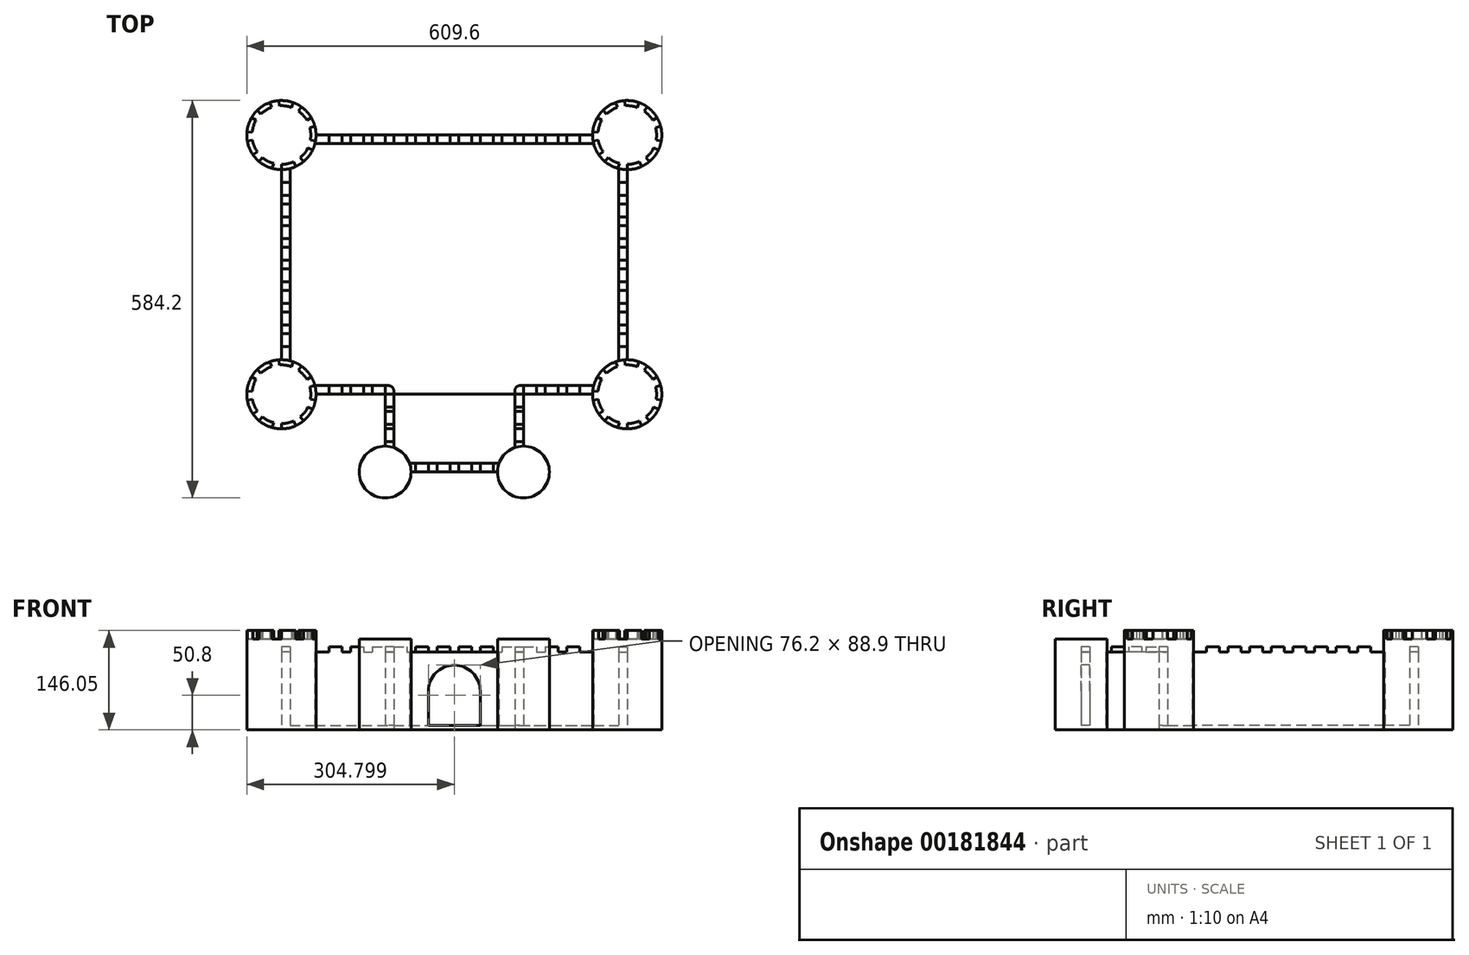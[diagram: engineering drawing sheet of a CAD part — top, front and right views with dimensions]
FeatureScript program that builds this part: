
annotation { "Feature Type Name" : "Feature", "Feature Type Description" : "" }
export const myFeature = defineFeature(function(context is Context, id is Id, definition is map)
    precondition{}
    {
        {
            var Q0;
            Q0=qCreatedBy(makeId("Top.planeOp"),FACE);
            var sketch = newSketch(context, id + "F0", { "sketchPlane" : qUnion([Q0])});
            skLineSegment(sketch, "E0.bottom", {"start": v(-131.16, 291.62) * mm, "end": v(376.84, 291.62) * mm});
            skLineSegment(sketch, "E0.top", {"start": v(-131.16, -89.38) * mm, "end": v(376.84, -89.38) * mm});
            skLineSegment(sketch, "E0.left", {"start": v(-131.16, 291.62) * mm, "end": v(-131.16, -89.38) * mm});
            skLineSegment(sketch, "E0.right", {"start": v(376.84, 291.62) * mm, "end": v(376.84, -89.38) * mm});
            skCircle(sketch, "E1", {"center": v(-131.16, 291.62) * mm, "radius": 50.8 * mm});
            skCircle(sketch, "E2", {"center": v(376.84, 291.62) * mm, "radius": 50.8 * mm});
            skCircle(sketch, "E3", {"center": v(-131.16, -89.38) * mm, "radius": 50.8 * mm});
            skCircle(sketch, "E4", {"center": v(376.84, -89.38) * mm, "radius": 50.8 * mm});
            skLineSegment(sketch, "E5.bottom", {"start": v(21.24, -89.38) * mm, "end": v(224.44, -89.38) * mm});
            skLineSegment(sketch, "E5.top", {"start": v(21.24, -203.68) * mm, "end": v(224.44, -203.68) * mm});
            skLineSegment(sketch, "E5.left", {"start": v(21.24, -89.38) * mm, "end": v(21.24, -203.68) * mm});
            skLineSegment(sketch, "E5.right", {"start": v(224.44, -89.38) * mm, "end": v(224.44, -203.68) * mm});
            skCircle(sketch, "E6", {"center": v(21.24, -203.68) * mm, "radius": 38.1 * mm});
            skCircle(sketch, "E7", {"center": v(224.44, -203.68) * mm, "radius": 38.1 * mm});
            skLineSegment(sketch, "E8.bottom", {"start": v(33.94, -89.38) * mm, "end": v(211.74, -89.38) * mm});
            skLineSegment(sketch, "E8.top", {"start": v(33.94, -190.98) * mm, "end": v(211.74, -190.98) * mm});
            skLineSegment(sketch, "E8.left", {"start": v(33.94, -89.38) * mm, "end": v(33.94, -190.98) * mm});
            skLineSegment(sketch, "E8.right", {"start": v(211.74, -89.38) * mm, "end": v(211.74, -190.98) * mm});
            skSolve(sketch);
        }
        {
            var Q0;
            {var subQ5=sQuery(id+"F0.wireOp",EDGE,"E1");var subQ10=sQuery(id+"F0.wireOp",EDGE,"E0.bottom");var subQ15=makeQuery(id+"F0.imprint","INTERSECT",VERTEX,{"derivedFrom":[subQ10,subQ5]});Q0=makeQuery(id+"F0.imprint","IMPRINT",FACE,{"disambiguationData":[TD([[makeQuery(id+"F0.imprint","IMPRINT",EDGE,{"disambiguationData":[TD([[subQ15,-1.0]])],"derivedFrom":subQ10}),-1.0]])]});}
            var Q1;
            {var subQ5=sQuery(id+"F0.wireOp",EDGE,"E8.bottom");Q1=makeQuery(id+"F0.imprint","IMPRINT",FACE,{"disambiguationData":[TD([[makeQuery(id+"F0.imprint","IMPRINT",EDGE,{"derivedFrom":subQ5}),-1.0]])]});}
            extrude(context, id + "F1", {"entities" : qUnion([Q0, Q1]), "depth" : 6.35 * mm});
        }
        {
            var Q0;
            {var subQ0=sQuery(id+"F0.wireOp",EDGE,"E0.left");var subQ1=sQuery(id+"F0.wireOp",EDGE,"E0.bottom");var subQ2=makeQuery(id+"F0.imprint","INTERSECT",VERTEX,{"derivedFrom":[subQ1,subQ0]});Q0=makeQuery(id+"F0.imprint","IMPRINT",FACE,{"disambiguationData":[TD([[makeQuery(id+"F0.imprint","IMPRINT",EDGE,{"disambiguationData":[TD([[subQ2,-1.0]])],"derivedFrom":subQ1}),1.0]])]});}
            var Q1;
            {var subQ0=sQuery(id+"F0.wireOp",EDGE,"E0.left");var subQ1=sQuery(id+"F0.wireOp",EDGE,"E0.bottom");var subQ2=makeQuery(id+"F0.imprint","INTERSECT",VERTEX,{"derivedFrom":[subQ1,subQ0]});Q1=makeQuery(id+"F0.imprint","IMPRINT",FACE,{"disambiguationData":[TD([[makeQuery(id+"F0.imprint","IMPRINT",EDGE,{"disambiguationData":[TD([[subQ2,-1.0]])],"derivedFrom":subQ1}),-1.0]])]});}
            var Q2;
            {var subQ0=sQuery(id+"F0.wireOp",EDGE,"E0.left");var subQ1=sQuery(id+"F0.wireOp",EDGE,"E0.top");var subQ2=makeQuery(id+"F0.imprint","INTERSECT",VERTEX,{"derivedFrom":[subQ1,subQ0]});Q2=makeQuery(id+"F0.imprint","IMPRINT",FACE,{"disambiguationData":[TD([[makeQuery(id+"F0.imprint","IMPRINT",EDGE,{"disambiguationData":[TD([[subQ2,-1.0]])],"derivedFrom":subQ1}),-1.0]])]});}
            var Q3;
            {var subQ0=sQuery(id+"F0.wireOp",EDGE,"E0.left");var subQ1=sQuery(id+"F0.wireOp",EDGE,"E0.top");var subQ2=makeQuery(id+"F0.imprint","INTERSECT",VERTEX,{"derivedFrom":[subQ1,subQ0]});Q3=makeQuery(id+"F0.imprint","IMPRINT",FACE,{"disambiguationData":[TD([[makeQuery(id+"F0.imprint","IMPRINT",EDGE,{"disambiguationData":[TD([[subQ2,-1.0]])],"derivedFrom":subQ1}),1.0]])]});}
            var Q4;
            {var subQ0=sQuery(id+"F0.wireOp",EDGE,"E0.right");var subQ1=sQuery(id+"F0.wireOp",EDGE,"E0.bottom");var subQ2=makeQuery(id+"F0.imprint","INTERSECT",VERTEX,{"derivedFrom":[subQ1,subQ0]});Q4=makeQuery(id+"F0.imprint","IMPRINT",FACE,{"disambiguationData":[TD([[makeQuery(id+"F0.imprint","IMPRINT",EDGE,{"disambiguationData":[TD([[subQ2,1.0]])],"derivedFrom":subQ1}),-1.0]])]});}
            var Q5;
            {var subQ0=sQuery(id+"F0.wireOp",EDGE,"E0.right");var subQ1=sQuery(id+"F0.wireOp",EDGE,"E0.bottom");var subQ2=makeQuery(id+"F0.imprint","INTERSECT",VERTEX,{"derivedFrom":[subQ1,subQ0]});Q5=makeQuery(id+"F0.imprint","IMPRINT",FACE,{"disambiguationData":[TD([[makeQuery(id+"F0.imprint","IMPRINT",EDGE,{"disambiguationData":[TD([[subQ2,1.0]])],"derivedFrom":subQ1}),1.0]])]});}
            var Q6;
            {var subQ0=sQuery(id+"F0.wireOp",EDGE,"E0.right");var subQ1=sQuery(id+"F0.wireOp",EDGE,"E0.top");var subQ2=makeQuery(id+"F0.imprint","INTERSECT",VERTEX,{"derivedFrom":[subQ1,subQ0]});Q6=makeQuery(id+"F0.imprint","IMPRINT",FACE,{"disambiguationData":[TD([[makeQuery(id+"F0.imprint","IMPRINT",EDGE,{"disambiguationData":[TD([[subQ2,1.0]])],"derivedFrom":subQ1}),-1.0]])]});}
            var Q7;
            {var subQ0=sQuery(id+"F0.wireOp",EDGE,"E0.right");var subQ1=sQuery(id+"F0.wireOp",EDGE,"E0.top");var subQ2=makeQuery(id+"F0.imprint","INTERSECT",VERTEX,{"derivedFrom":[subQ1,subQ0]});Q7=makeQuery(id+"F0.imprint","IMPRINT",FACE,{"disambiguationData":[TD([[makeQuery(id+"F0.imprint","IMPRINT",EDGE,{"disambiguationData":[TD([[subQ2,1.0]])],"derivedFrom":subQ1}),1.0]])]});}
            extrude(context, id + "F2", {"entities" : qUnion([Q0, Q1, Q2, Q3, Q4, Q5, Q6, Q7]), "operationType" : NewBodyOperationType.ADD, "depth" : 133.35 * mm});
        }
        {
            var Q0;
            Q0=makeQuery(id+"F1.opExtrude","CAP_FACE",FACE,{"disambiguationData":[OSD([sQuery(id+"F0.wireOp",EDGE,"E0.bottom"),sQuery(id+"F0.wireOp",EDGE,"E0.top"),sQuery(id+"F0.wireOp",EDGE,"E0.left"),sQuery(id+"F0.wireOp",EDGE,"E0.right"),sQuery(id+"F0.wireOp",EDGE,"E1"),sQuery(id+"F0.wireOp",EDGE,"E2"),sQuery(id+"F0.wireOp",EDGE,"E3"),sQuery(id+"F0.wireOp",EDGE,"E4")])],"isStart":false});
            var sketch = newSketch(context, id + "F3", { "sketchPlane" : qUnion([Q0])});
            skLineSegment(sketch, "E9", {"start": v(-80.36, -89.38) * mm, "end": v(326.04, -89.38) * mm});
            skLineSegment(sketch, "E10", {"start": v(-118.46, 242.43) * mm, "end": v(-118.46, -40.2) * mm});
            skLineSegment(sketch, "E11", {"start": v(-131.16, 240.82) * mm, "end": v(-131.16, -38.58) * mm});
            skLineSegment(sketch, "E12", {"start": v(-80.36, 291.62) * mm, "end": v(326.04, 291.62) * mm});
            skLineSegment(sketch, "E13", {"start": v(-81.97, 278.92) * mm, "end": v(327.65, 278.92) * mm});
            skLineSegment(sketch, "E14", {"start": v(376.84, 240.82) * mm, "end": v(376.84, -38.58) * mm});
            skLineSegment(sketch, "E15", {"start": v(364.14, 242.43) * mm, "end": v(364.14, -40.2) * mm});
            skLineSegment(sketch, "E16", {"start": v(-81.97, -76.68) * mm, "end": v(33.94, -76.68) * mm});
            skLineSegment(sketch, "E17", {"start": v(33.94, -76.68) * mm, "end": v(33.94, -89.38) * mm});
            skLineSegment(sketch, "E18", {"start": v(211.74, -89.38) * mm, "end": v(211.74, -76.68) * mm});
            skLineSegment(sketch, "E19", {"start": v(211.74, -76.68) * mm, "end": v(327.65, -76.68) * mm});
            skSolve(sketch);
        }
        {
            var Q0;
            {var subQ0=sQuery(id+"F3.wireOp",EDGE,"E10");Q0=makeQuery(id+"F3.imprint","IMPRINT",FACE,{"disambiguationData":[TD([[makeQuery(id+"F3.imprint","IMPRINT",EDGE,{"derivedFrom":subQ0}),-1.0]])]});}
            var Q1;
            {var subQ0=sQuery(id+"F3.wireOp",EDGE,"9q2WOOh6-w2Ju-GZx3-tS78-7SEucZNv8yoA");Q1=makeQuery(id+"F3.imprint","IMPRINT",FACE,{"disambiguationData":[TD([[makeQuery(id+"F3.imprint","IMPRINT",EDGE,{"derivedFrom":subQ0}),-1.0]])]});}
            var Q2;
            {var subQ0=sQuery(id+"F3.wireOp",EDGE,"E14");Q2=makeQuery(id+"F3.imprint","IMPRINT",FACE,{"disambiguationData":[TD([[makeQuery(id+"F3.imprint","IMPRINT",EDGE,{"derivedFrom":subQ0}),-1.0]])]});}
            var Q3;
            {var subQ0=sQuery(id+"F3.wireOp",EDGE,"E12");Q3=makeQuery(id+"F3.imprint","IMPRINT",FACE,{"disambiguationData":[TD([[makeQuery(id+"F3.imprint","IMPRINT",EDGE,{"derivedFrom":subQ0}),-1.0]])]});}
            var Q4;
            {var subQ4=sQuery(id+"F3.wireOp",EDGE,"E16");Q4=makeQuery(id+"F3.imprint","IMPRINT",FACE,{"disambiguationData":[TD([[makeQuery(id+"F3.imprint","IMPRINT",EDGE,{"derivedFrom":subQ4}),-1.0]])]});}
            var Q5;
            {var subQ0=sQuery(id+"F3.wireOp",EDGE,"E18");Q5=makeQuery(id+"F3.imprint","IMPRINT",FACE,{"disambiguationData":[TD([[makeQuery(id+"F3.imprint","IMPRINT",EDGE,{"derivedFrom":subQ0}),-1.0]])]});}
            extrude(context, id + "F4", {"entities" : qUnion([Q0, Q1, Q2, Q3, Q4, Q5]), "operationType" : NewBodyOperationType.ADD, "depth" : 107.95 * mm});
        }
        {
            var Q0;
            Q0=makeQuery(id+"F4.opExtrude","CAP_FACE",FACE,{"disambiguationData":[OSD([sQuery(id+"F0.wireOp",EDGE,"E3"),sQuery(id+"F0.wireOp",EDGE,"E4"),sQuery(id+"F3.wireOp",EDGE,"9q2WOOh6-w2Ju-GZx3-tS78-7SEucZNv8yoA"),sQuery(id+"F3.wireOp",EDGE,"E9")])],"isStart":false});
            var sketch = newSketch(context, id + "F5", { "sketchPlane" : qUnion([Q0])});
            skLineSegment(sketch, "E20.bottom", {"start": v(-61.31, -76.68) * mm, "end": v(-42.26, -76.68) * mm});
            skLineSegment(sketch, "E20.top", {"start": v(-61.31, -89.38) * mm, "end": v(-42.26, -89.38) * mm});
            skLineSegment(sketch, "E20.left", {"start": v(-61.31, -76.68) * mm, "end": v(-61.31, -89.38) * mm});
            skLineSegment(sketch, "E20.right", {"start": v(-42.26, -76.68) * mm, "end": v(-42.26, -89.38) * mm});
            skLineSegment(sketch, "E21.bottom", {"start": v(-29.56, -76.68) * mm, "end": v(-10.51, -76.68) * mm});
            skLineSegment(sketch, "E21.top", {"start": v(-29.56, -89.38) * mm, "end": v(-10.51, -89.38) * mm});
            skLineSegment(sketch, "E21.left", {"start": v(-29.56, -76.68) * mm, "end": v(-29.56, -89.38) * mm});
            skLineSegment(sketch, "E21.right", {"start": v(-10.51, -76.68) * mm, "end": v(-10.51, -89.38) * mm});
            skLineSegment(sketch, "E22.bottom", {"start": v(2.19, -76.68) * mm, "end": v(21.24, -76.68) * mm});
            skLineSegment(sketch, "E22.top", {"start": v(2.19, -89.38) * mm, "end": v(21.24, -89.38) * mm});
            skLineSegment(sketch, "E22.left", {"start": v(2.19, -76.68) * mm, "end": v(2.19, -89.38) * mm});
            skLineSegment(sketch, "E22.right", {"start": v(21.24, -76.68) * mm, "end": v(21.24, -89.38) * mm});
            skLineSegment(sketch, "E23.bottom", {"start": v(224.44, -76.68) * mm, "end": v(243.49, -76.68) * mm});
            skLineSegment(sketch, "E23.top", {"start": v(224.44, -89.38) * mm, "end": v(243.49, -89.38) * mm});
            skLineSegment(sketch, "E23.left", {"start": v(224.44, -76.68) * mm, "end": v(224.44, -89.38) * mm});
            skLineSegment(sketch, "E23.right", {"start": v(243.49, -76.68) * mm, "end": v(243.49, -89.38) * mm});
            skLineSegment(sketch, "E24.bottom", {"start": v(256.19, -76.68) * mm, "end": v(275.24, -76.68) * mm});
            skLineSegment(sketch, "E24.top", {"start": v(256.19, -89.38) * mm, "end": v(275.24, -89.38) * mm});
            skLineSegment(sketch, "E24.left", {"start": v(256.19, -76.68) * mm, "end": v(256.19, -89.38) * mm});
            skLineSegment(sketch, "E24.right", {"start": v(275.24, -76.68) * mm, "end": v(275.24, -89.38) * mm});
            skLineSegment(sketch, "E25.bottom", {"start": v(287.94, -76.68) * mm, "end": v(306.99, -76.68) * mm});
            skLineSegment(sketch, "E25.top", {"start": v(287.94, -89.38) * mm, "end": v(306.99, -89.38) * mm});
            skLineSegment(sketch, "E25.left", {"start": v(287.94, -76.68) * mm, "end": v(287.94, -89.38) * mm});
            skLineSegment(sketch, "E25.right", {"start": v(306.99, -76.68) * mm, "end": v(306.99, -89.38) * mm});
            skSolve(sketch);
        }
        {
            var Q0;
            Q0 = qSketchRegion(id + "F5", true);
            extrude(context, id + "F6", {"entities" : qUnion([Q0]), "operationType" : NewBodyOperationType.ADD, "depth" : 7.62 * mm});
        }
        {
            var Q0;
            Q0=makeQuery(id+"F4.opExtrude","CAP_FACE",FACE,{"disambiguationData":[OSD([sQuery(id+"F0.wireOp",EDGE,"E1"),sQuery(id+"F0.wireOp",EDGE,"E3"),sQuery(id+"F3.wireOp",EDGE,"E10"),sQuery(id+"F3.wireOp",EDGE,"E11")])],"isStart":false});
            var sketch = newSketch(context, id + "F7", { "sketchPlane" : qUnion([Q0])});
            skLineSegment(sketch, "E26.bottom", {"start": v(-118.46, 221.77) * mm, "end": v(-131.16, 221.77) * mm});
            skLineSegment(sketch, "E26.top", {"start": v(-118.46, 202.72) * mm, "end": v(-131.16, 202.72) * mm});
            skLineSegment(sketch, "E26.left", {"start": v(-118.46, 221.77) * mm, "end": v(-118.46, 202.72) * mm});
            skLineSegment(sketch, "E26.right", {"start": v(-131.16, 221.77) * mm, "end": v(-131.16, 202.72) * mm});
            skLineSegment(sketch, "E27.bottom", {"start": v(-118.46, 190.02) * mm, "end": v(-131.16, 190.02) * mm});
            skLineSegment(sketch, "E27.top", {"start": v(-118.46, 170.97) * mm, "end": v(-131.16, 170.97) * mm});
            skLineSegment(sketch, "E27.left", {"start": v(-118.46, 190.02) * mm, "end": v(-118.46, 170.97) * mm});
            skLineSegment(sketch, "E27.right", {"start": v(-131.16, 190.02) * mm, "end": v(-131.16, 170.97) * mm});
            skLineSegment(sketch, "E28.bottom", {"start": v(-118.46, 158.27) * mm, "end": v(-131.16, 158.27) * mm});
            skLineSegment(sketch, "E28.top", {"start": v(-118.46, 139.22) * mm, "end": v(-131.16, 139.22) * mm});
            skLineSegment(sketch, "E28.left", {"start": v(-118.46, 158.27) * mm, "end": v(-118.46, 139.22) * mm});
            skLineSegment(sketch, "E28.right", {"start": v(-131.16, 158.27) * mm, "end": v(-131.16, 139.22) * mm});
            skLineSegment(sketch, "E29.bottom", {"start": v(-118.46, 126.52) * mm, "end": v(-131.16, 126.52) * mm});
            skLineSegment(sketch, "E29.top", {"start": v(-118.46, 107.47) * mm, "end": v(-131.16, 107.47) * mm});
            skLineSegment(sketch, "E29.left", {"start": v(-118.46, 126.52) * mm, "end": v(-118.46, 107.47) * mm});
            skLineSegment(sketch, "E29.right", {"start": v(-131.16, 126.52) * mm, "end": v(-131.16, 107.47) * mm});
            skLineSegment(sketch, "E30.bottom", {"start": v(-118.46, 94.77) * mm, "end": v(-131.16, 94.77) * mm});
            skLineSegment(sketch, "E30.top", {"start": v(-118.46, 75.72) * mm, "end": v(-131.16, 75.72) * mm});
            skLineSegment(sketch, "E30.left", {"start": v(-118.46, 94.77) * mm, "end": v(-118.46, 75.72) * mm});
            skLineSegment(sketch, "E30.right", {"start": v(-131.16, 94.77) * mm, "end": v(-131.16, 75.72) * mm});
            skLineSegment(sketch, "E31.bottom", {"start": v(-118.46, 63.02) * mm, "end": v(-131.16, 63.02) * mm});
            skLineSegment(sketch, "E31.top", {"start": v(-118.46, 43.97) * mm, "end": v(-131.16, 43.97) * mm});
            skLineSegment(sketch, "E31.left", {"start": v(-118.46, 63.02) * mm, "end": v(-118.46, 43.97) * mm});
            skLineSegment(sketch, "E31.right", {"start": v(-131.16, 63.02) * mm, "end": v(-131.16, 43.97) * mm});
            skLineSegment(sketch, "E32.bottom", {"start": v(-118.46, 31.27) * mm, "end": v(-131.16, 31.27) * mm});
            skLineSegment(sketch, "E32.top", {"start": v(-118.46, 12.22) * mm, "end": v(-131.16, 12.22) * mm});
            skLineSegment(sketch, "E32.left", {"start": v(-118.46, 31.27) * mm, "end": v(-118.46, 12.22) * mm});
            skLineSegment(sketch, "E32.right", {"start": v(-131.16, 31.27) * mm, "end": v(-131.16, 12.22) * mm});
            skLineSegment(sketch, "E33.bottom", {"start": v(-118.46, -0.48) * mm, "end": v(-131.16, -0.48) * mm});
            skLineSegment(sketch, "E33.top", {"start": v(-118.46, -19.53) * mm, "end": v(-131.16, -19.53) * mm});
            skLineSegment(sketch, "E33.left", {"start": v(-118.46, -0.48) * mm, "end": v(-118.46, -19.53) * mm});
            skLineSegment(sketch, "E33.right", {"start": v(-131.16, -0.48) * mm, "end": v(-131.16, -19.53) * mm});
            skSolve(sketch);
        }
        {
            var Q0;
            Q0 = qSketchRegion(id + "F7", true);
            extrude(context, id + "F8", {"entities" : qUnion([Q0]), "operationType" : NewBodyOperationType.ADD, "depth" : 7.62 * mm});
        }
        {
            var Q0;
            Q0=makeQuery(id+"F4.opExtrude","CAP_FACE",FACE,{"disambiguationData":[OSD([sQuery(id+"F0.wireOp",EDGE,"E1"),sQuery(id+"F0.wireOp",EDGE,"E2"),sQuery(id+"F3.wireOp",EDGE,"E12"),sQuery(id+"F3.wireOp",EDGE,"E13")])],"isStart":false});
            var sketch = newSketch(context, id + "F9", { "sketchPlane" : qUnion([Q0])});
            skLineSegment(sketch, "E34.bottom", {"start": v(-61.31, 291.62) * mm, "end": v(-42.26, 291.62) * mm});
            skLineSegment(sketch, "E34.top", {"start": v(-61.31, 278.92) * mm, "end": v(-42.26, 278.92) * mm});
            skLineSegment(sketch, "E34.left", {"start": v(-61.31, 291.62) * mm, "end": v(-61.31, 278.92) * mm});
            skLineSegment(sketch, "E34.right", {"start": v(-42.26, 291.62) * mm, "end": v(-42.26, 278.92) * mm});
            skLineSegment(sketch, "E35.bottom", {"start": v(-29.56, 291.62) * mm, "end": v(-10.51, 291.62) * mm});
            skLineSegment(sketch, "E35.top", {"start": v(-29.56, 278.92) * mm, "end": v(-10.51, 278.92) * mm});
            skLineSegment(sketch, "E35.left", {"start": v(-29.56, 291.62) * mm, "end": v(-29.56, 278.92) * mm});
            skLineSegment(sketch, "E35.right", {"start": v(-10.51, 291.62) * mm, "end": v(-10.51, 278.92) * mm});
            skLineSegment(sketch, "E36.bottom", {"start": v(2.19, 291.62) * mm, "end": v(21.24, 291.62) * mm});
            skLineSegment(sketch, "E36.top", {"start": v(2.19, 278.92) * mm, "end": v(21.24, 278.92) * mm});
            skLineSegment(sketch, "E36.left", {"start": v(2.19, 291.62) * mm, "end": v(2.19, 278.92) * mm});
            skLineSegment(sketch, "E36.right", {"start": v(21.24, 291.62) * mm, "end": v(21.24, 278.92) * mm});
            skLineSegment(sketch, "E37.bottom", {"start": v(33.94, 291.62) * mm, "end": v(52.99, 291.62) * mm});
            skLineSegment(sketch, "E37.top", {"start": v(33.94, 278.92) * mm, "end": v(52.99, 278.92) * mm});
            skLineSegment(sketch, "E37.left", {"start": v(33.94, 291.62) * mm, "end": v(33.94, 278.92) * mm});
            skLineSegment(sketch, "E37.right", {"start": v(52.99, 291.62) * mm, "end": v(52.99, 278.92) * mm});
            skLineSegment(sketch, "E38.bottom", {"start": v(65.69, 291.62) * mm, "end": v(84.74, 291.62) * mm});
            skLineSegment(sketch, "E38.top", {"start": v(65.69, 278.92) * mm, "end": v(84.74, 278.92) * mm});
            skLineSegment(sketch, "E38.left", {"start": v(65.69, 291.62) * mm, "end": v(65.69, 278.92) * mm});
            skLineSegment(sketch, "E38.right", {"start": v(84.74, 291.62) * mm, "end": v(84.74, 278.92) * mm});
            skLineSegment(sketch, "E39.bottom", {"start": v(97.44, 291.62) * mm, "end": v(116.49, 291.62) * mm});
            skLineSegment(sketch, "E39.top", {"start": v(97.44, 278.92) * mm, "end": v(116.49, 278.92) * mm});
            skLineSegment(sketch, "E39.left", {"start": v(97.44, 291.62) * mm, "end": v(97.44, 278.92) * mm});
            skLineSegment(sketch, "E39.right", {"start": v(116.49, 291.62) * mm, "end": v(116.49, 278.92) * mm});
            skLineSegment(sketch, "E40.bottom", {"start": v(129.19, 291.62) * mm, "end": v(148.24, 291.62) * mm});
            skLineSegment(sketch, "E40.top", {"start": v(129.19, 278.92) * mm, "end": v(148.24, 278.92) * mm});
            skLineSegment(sketch, "E40.left", {"start": v(129.19, 291.62) * mm, "end": v(129.19, 278.92) * mm});
            skLineSegment(sketch, "E40.right", {"start": v(148.24, 291.62) * mm, "end": v(148.24, 278.92) * mm});
            skLineSegment(sketch, "E41.bottom", {"start": v(160.94, 291.62) * mm, "end": v(179.99, 291.62) * mm});
            skLineSegment(sketch, "E41.top", {"start": v(160.94, 278.92) * mm, "end": v(179.99, 278.92) * mm});
            skLineSegment(sketch, "E41.left", {"start": v(160.94, 291.62) * mm, "end": v(160.94, 278.92) * mm});
            skLineSegment(sketch, "E41.right", {"start": v(179.99, 291.62) * mm, "end": v(179.99, 278.92) * mm});
            skLineSegment(sketch, "E42.bottom", {"start": v(192.69, 291.62) * mm, "end": v(211.74, 291.62) * mm});
            skLineSegment(sketch, "E42.top", {"start": v(192.69, 278.92) * mm, "end": v(211.74, 278.92) * mm});
            skLineSegment(sketch, "E42.left", {"start": v(192.69, 291.62) * mm, "end": v(192.69, 278.92) * mm});
            skLineSegment(sketch, "E42.right", {"start": v(211.74, 291.62) * mm, "end": v(211.74, 278.92) * mm});
            skLineSegment(sketch, "E43.bottom", {"start": v(224.44, 291.62) * mm, "end": v(243.49, 291.62) * mm});
            skLineSegment(sketch, "E43.top", {"start": v(224.44, 278.92) * mm, "end": v(243.49, 278.92) * mm});
            skLineSegment(sketch, "E43.left", {"start": v(224.44, 291.62) * mm, "end": v(224.44, 278.92) * mm});
            skLineSegment(sketch, "E43.right", {"start": v(243.49, 291.62) * mm, "end": v(243.49, 278.92) * mm});
            skLineSegment(sketch, "E44.bottom", {"start": v(256.19, 291.62) * mm, "end": v(275.24, 291.62) * mm});
            skLineSegment(sketch, "E44.top", {"start": v(256.19, 278.92) * mm, "end": v(275.24, 278.92) * mm});
            skLineSegment(sketch, "E44.left", {"start": v(256.19, 291.62) * mm, "end": v(256.19, 278.92) * mm});
            skLineSegment(sketch, "E44.right", {"start": v(275.24, 291.62) * mm, "end": v(275.24, 278.92) * mm});
            skLineSegment(sketch, "E45.bottom", {"start": v(287.94, 291.62) * mm, "end": v(306.99, 291.62) * mm});
            skLineSegment(sketch, "E45.top", {"start": v(287.94, 278.92) * mm, "end": v(306.99, 278.92) * mm});
            skLineSegment(sketch, "E45.left", {"start": v(287.94, 291.62) * mm, "end": v(287.94, 278.92) * mm});
            skLineSegment(sketch, "E45.right", {"start": v(306.99, 291.62) * mm, "end": v(306.99, 278.92) * mm});
            skSolve(sketch);
        }
        {
            var Q0;
            Q0 = qSketchRegion(id + "F9", true);
            extrude(context, id + "F10", {"entities" : qUnion([Q0]), "operationType" : NewBodyOperationType.ADD, "depth" : 7.62 * mm});
        }
        {
            var Q0;
            Q0=makeQuery(id+"F4.opExtrude","CAP_FACE",FACE,{"disambiguationData":[OSD([sQuery(id+"F0.wireOp",EDGE,"E2"),sQuery(id+"F0.wireOp",EDGE,"E4"),sQuery(id+"F3.wireOp",EDGE,"E14"),sQuery(id+"F3.wireOp",EDGE,"E15")])],"isStart":false});
            var sketch = newSketch(context, id + "F11", { "sketchPlane" : qUnion([Q0])});
            skLineSegment(sketch, "E46.bottom", {"start": v(364.14, -19.53) * mm, "end": v(376.84, -19.53) * mm});
            skLineSegment(sketch, "E46.top", {"start": v(364.14, -0.48) * mm, "end": v(376.84, -0.48) * mm});
            skLineSegment(sketch, "E46.left", {"start": v(364.14, -19.53) * mm, "end": v(364.14, -0.48) * mm});
            skLineSegment(sketch, "E46.right", {"start": v(376.84, -19.53) * mm, "end": v(376.84, -0.48) * mm});
            skLineSegment(sketch, "E47.bottom", {"start": v(364.14, 12.22) * mm, "end": v(376.84, 12.22) * mm});
            skLineSegment(sketch, "E47.top", {"start": v(364.14, 31.27) * mm, "end": v(376.84, 31.27) * mm});
            skLineSegment(sketch, "E47.left", {"start": v(364.14, 12.22) * mm, "end": v(364.14, 31.27) * mm});
            skLineSegment(sketch, "E47.right", {"start": v(376.84, 12.22) * mm, "end": v(376.84, 31.27) * mm});
            skLineSegment(sketch, "E48.bottom", {"start": v(364.14, 63.02) * mm, "end": v(376.84, 63.02) * mm});
            skLineSegment(sketch, "E48.top", {"start": v(364.14, 43.97) * mm, "end": v(376.84, 43.97) * mm});
            skLineSegment(sketch, "E48.left", {"start": v(364.14, 43.97) * mm, "end": v(364.14, 63.02) * mm});
            skLineSegment(sketch, "E48.right", {"start": v(376.84, 43.97) * mm, "end": v(376.84, 63.02) * mm});
            skLineSegment(sketch, "E49.bottom", {"start": v(364.14, 94.77) * mm, "end": v(376.84, 94.77) * mm});
            skLineSegment(sketch, "E49.top", {"start": v(364.14, 75.72) * mm, "end": v(376.84, 75.72) * mm});
            skLineSegment(sketch, "E49.left", {"start": v(364.14, 75.72) * mm, "end": v(364.14, 94.77) * mm});
            skLineSegment(sketch, "E49.right", {"start": v(376.84, 75.72) * mm, "end": v(376.84, 94.77) * mm});
            skLineSegment(sketch, "E50.bottom", {"start": v(364.14, 107.47) * mm, "end": v(376.84, 107.47) * mm});
            skLineSegment(sketch, "E50.top", {"start": v(364.14, 126.52) * mm, "end": v(376.84, 126.52) * mm});
            skLineSegment(sketch, "E50.left", {"start": v(364.14, 107.47) * mm, "end": v(364.14, 126.52) * mm});
            skLineSegment(sketch, "E50.right", {"start": v(376.84, 107.47) * mm, "end": v(376.84, 126.52) * mm});
            skLineSegment(sketch, "E51.bottom", {"start": v(364.14, 139.22) * mm, "end": v(376.84, 139.22) * mm});
            skLineSegment(sketch, "E51.top", {"start": v(364.14, 158.27) * mm, "end": v(376.84, 158.27) * mm});
            skLineSegment(sketch, "E51.left", {"start": v(364.14, 139.22) * mm, "end": v(364.14, 158.27) * mm});
            skLineSegment(sketch, "E51.right", {"start": v(376.84, 139.22) * mm, "end": v(376.84, 158.27) * mm});
            skLineSegment(sketch, "E52.bottom", {"start": v(364.14, 170.97) * mm, "end": v(376.84, 170.97) * mm});
            skLineSegment(sketch, "E52.top", {"start": v(364.14, 190.02) * mm, "end": v(376.84, 190.02) * mm});
            skLineSegment(sketch, "E52.left", {"start": v(364.14, 170.97) * mm, "end": v(364.14, 190.02) * mm});
            skLineSegment(sketch, "E52.right", {"start": v(376.84, 170.97) * mm, "end": v(376.84, 190.02) * mm});
            skLineSegment(sketch, "E53.bottom", {"start": v(364.14, 202.72) * mm, "end": v(376.84, 202.72) * mm});
            skLineSegment(sketch, "E53.top", {"start": v(364.14, 221.77) * mm, "end": v(376.84, 221.77) * mm});
            skLineSegment(sketch, "E53.left", {"start": v(364.14, 202.72) * mm, "end": v(364.14, 221.77) * mm});
            skLineSegment(sketch, "E53.right", {"start": v(376.84, 202.72) * mm, "end": v(376.84, 221.77) * mm});
            skSolve(sketch);
        }
        {
            var Q0;
            Q0 = qSketchRegion(id + "F11", true);
            extrude(context, id + "F12", {"entities" : qUnion([Q0]), "operationType" : NewBodyOperationType.ADD, "depth" : 7.62 * mm});
        }
        {
            var Q0;
            Q0=makeQuery(id+"F2.opExtrude","CAP_FACE",FACE,{"disambiguationData":[OSD([sQuery(id+"F0.wireOp",EDGE,"E1")])],"isStart":false});
            var sketch = newSketch(context, id + "F13", { "sketchPlane" : qUnion([Q0])});
            skCircle(sketch, "E54", {"center": v(-131.16, 291.62) * mm, "radius": 43.18 * mm});
            skLineSegment(sketch, "E55", {"start": v(-105.97, 326.69) * mm, "end": v(-101.52, 332.88) * mm});
            skLineSegment(sketch, "E56", {"start": v(-93.8, 313.27) * mm, "end": v(-87.21, 317.1) * mm});
            skLineSegment(sketch, "E57", {"start": v(-113.65, 339.3) * mm, "end": v(-116.28, 332.15) * mm});
            skLineSegment(sketch, "E58", {"start": v(-135, 342.27) * mm, "end": v(-134.43, 334.68) * mm});
            skLineSegment(sketch, "E59", {"start": v(-148.43, 339.4) * mm, "end": v(-145.84, 332.23) * mm});
            skLineSegment(sketch, "E60", {"start": v(-166.68, 327.93) * mm, "end": v(-161.36, 322.49) * mm});
            skLineSegment(sketch, "E61", {"start": v(-175.11, 317.1) * mm, "end": v(-168.52, 313.27) * mm});
            skLineSegment(sketch, "E62", {"start": v(-181.72, 296.58) * mm, "end": v(-174.13, 295.83) * mm});
            skLineSegment(sketch, "E63", {"start": v(-173.7, 284.17) * mm, "end": v(-181.2, 282.86) * mm});
            skLineSegment(sketch, "E64", {"start": v(-173.06, 262.9) * mm, "end": v(-166.77, 267.2) * mm});
            skLineSegment(sketch, "E65", {"start": v(-163.84, 252.72) * mm, "end": v(-158.94, 258.56) * mm});
            skLineSegment(sketch, "E66", {"start": v(-142.72, 250.02) * mm, "end": v(-144.76, 242.68) * mm});
            skLineSegment(sketch, "E67", {"start": v(-131.16, 248.44) * mm, "end": v(-131.16, 240.82) * mm});
            skLineSegment(sketch, "E68", {"start": v(-113.25, 252.33) * mm, "end": v(-110.1, 245.4) * mm});
            skLineSegment(sketch, "E69", {"start": v(-103.39, 258.56) * mm, "end": v(-98.48, 252.72) * mm});
            skLineSegment(sketch, "E70", {"start": v(-92.18, 273.05) * mm, "end": v(-85.3, 269.78) * mm});
            skLineSegment(sketch, "E71", {"start": v(-88.63, 284.17) * mm, "end": v(-81.12, 282.86) * mm});
            skLineSegment(sketch, "E72", {"start": v(-89.37, 302.48) * mm, "end": v(-82, 304.4) * mm});
            skSolve(sketch);
        }
        {
            var Q0;
            {var subQ0=sQuery(id+"F13.wireOp",EDGE,"E59");Q0=makeQuery(id+"F13.imprint","IMPRINT",FACE,{"disambiguationData":[TD([[makeQuery(id+"F13.imprint","IMPRINT",EDGE,{"derivedFrom":subQ0}),-1.0]])]});}
            var Q1;
            {var subQ0=sQuery(id+"F13.wireOp",EDGE,"E57");Q1=makeQuery(id+"F13.imprint","IMPRINT",FACE,{"disambiguationData":[TD([[makeQuery(id+"F13.imprint","IMPRINT",EDGE,{"derivedFrom":subQ0}),-1.0]])]});}
            var Q2;
            {var subQ0=sQuery(id+"F13.wireOp",EDGE,"E55");Q2=makeQuery(id+"F13.imprint","IMPRINT",FACE,{"disambiguationData":[TD([[makeQuery(id+"F13.imprint","IMPRINT",EDGE,{"derivedFrom":subQ0}),-1.0]])]});}
            var Q3;
            {var subQ0=sQuery(id+"F13.wireOp",EDGE,"E71");Q3=makeQuery(id+"F13.imprint","IMPRINT",FACE,{"disambiguationData":[TD([[makeQuery(id+"F13.imprint","IMPRINT",EDGE,{"derivedFrom":subQ0}),1.0]])]});}
            var Q4;
            {var subQ0=sQuery(id+"F13.wireOp",EDGE,"E69");Q4=makeQuery(id+"F13.imprint","IMPRINT",FACE,{"disambiguationData":[TD([[makeQuery(id+"F13.imprint","IMPRINT",EDGE,{"derivedFrom":subQ0}),1.0]])]});}
            var Q5;
            {var subQ0=sQuery(id+"F13.wireOp",EDGE,"E67");Q5=makeQuery(id+"F13.imprint","IMPRINT",FACE,{"disambiguationData":[TD([[makeQuery(id+"F13.imprint","IMPRINT",EDGE,{"derivedFrom":subQ0}),1.0]])]});}
            var Q6;
            {var subQ0=sQuery(id+"F13.wireOp",EDGE,"E65");Q6=makeQuery(id+"F13.imprint","IMPRINT",FACE,{"disambiguationData":[TD([[makeQuery(id+"F13.imprint","IMPRINT",EDGE,{"derivedFrom":subQ0}),-1.0]])]});}
            var Q7;
            {var subQ0=sQuery(id+"F13.wireOp",EDGE,"E63");Q7=makeQuery(id+"F13.imprint","IMPRINT",FACE,{"disambiguationData":[TD([[makeQuery(id+"F13.imprint","IMPRINT",EDGE,{"derivedFrom":subQ0}),1.0]])]});}
            var Q8;
            {var subQ0=sQuery(id+"F13.wireOp",EDGE,"E61");Q8=makeQuery(id+"F13.imprint","IMPRINT",FACE,{"disambiguationData":[TD([[makeQuery(id+"F13.imprint","IMPRINT",EDGE,{"derivedFrom":subQ0}),-1.0]])]});}
            extrude(context, id + "F14", {"entities" : qUnion([Q0, Q1, Q2, Q3, Q4, Q5, Q6, Q7, Q8]), "operationType" : NewBodyOperationType.ADD, "depth" : 12.7 * mm});
        }
        {
            var Q0;
            Q0=makeQuery(id+"F2.opExtrude","CAP_FACE",FACE,{"disambiguationData":[OSD([sQuery(id+"F0.wireOp",EDGE,"E2")])],"isStart":false});
            var sketch = newSketch(context, id + "F15", { "sketchPlane" : qUnion([Q0])});
            skCircle(sketch, "E73", {"center": v(376.84, 291.62) * mm, "radius": 43.18 * mm});
            skLineSegment(sketch, "E74", {"start": v(402.03, 326.69) * mm, "end": v(406.48, 332.88) * mm});
            skLineSegment(sketch, "E75", {"start": v(414.2, 313.27) * mm, "end": v(420.79, 317.1) * mm});
            skLineSegment(sketch, "E76", {"start": v(394.35, 339.3) * mm, "end": v(391.72, 332.15) * mm});
            skLineSegment(sketch, "E77", {"start": v(373, 342.27) * mm, "end": v(373.57, 334.68) * mm});
            skLineSegment(sketch, "E78", {"start": v(359.57, 339.4) * mm, "end": v(362.16, 332.23) * mm});
            skLineSegment(sketch, "E79", {"start": v(341.32, 327.93) * mm, "end": v(346.64, 322.49) * mm});
            skLineSegment(sketch, "E80", {"start": v(332.89, 317.1) * mm, "end": v(339.48, 313.27) * mm});
            skLineSegment(sketch, "E81", {"start": v(326.28, 296.58) * mm, "end": v(333.87, 295.83) * mm});
            skLineSegment(sketch, "E82", {"start": v(334.3, 284.17) * mm, "end": v(326.8, 282.86) * mm});
            skLineSegment(sketch, "E83", {"start": v(334.94, 262.9) * mm, "end": v(341.23, 267.2) * mm});
            skLineSegment(sketch, "E84", {"start": v(344.16, 252.72) * mm, "end": v(349.06, 258.56) * mm});
            skLineSegment(sketch, "E85", {"start": v(365.28, 250.02) * mm, "end": v(363.24, 242.68) * mm});
            skLineSegment(sketch, "E86", {"start": v(376.84, 248.44) * mm, "end": v(376.84, 239.8) * mm});
            skLineSegment(sketch, "E87", {"start": v(394.75, 252.33) * mm, "end": v(397.9, 245.4) * mm});
            skLineSegment(sketch, "E88", {"start": v(404.61, 258.56) * mm, "end": v(409.52, 252.72) * mm});
            skLineSegment(sketch, "E89", {"start": v(415.82, 273.05) * mm, "end": v(422.7, 269.78) * mm});
            skLineSegment(sketch, "E90", {"start": v(419.37, 284.17) * mm, "end": v(426.88, 282.86) * mm});
            skLineSegment(sketch, "E91", {"start": v(418.63, 302.48) * mm, "end": v(426, 304.4) * mm});
            skSolve(sketch);
        }
        {
            var Q0;
            {var subQ0=sQuery(id+"F15.wireOp",EDGE,"E74");Q0=makeQuery(id+"F15.imprint","IMPRINT",FACE,{"disambiguationData":[TD([[makeQuery(id+"F15.imprint","IMPRINT",EDGE,{"derivedFrom":subQ0}),-1.0]])]});}
            var Q1;
            {var subQ0=sQuery(id+"F15.wireOp",EDGE,"E76");Q1=makeQuery(id+"F15.imprint","IMPRINT",FACE,{"disambiguationData":[TD([[makeQuery(id+"F15.imprint","IMPRINT",EDGE,{"derivedFrom":subQ0}),-1.0]])]});}
            var Q2;
            {var subQ0=sQuery(id+"F15.wireOp",EDGE,"E78");Q2=makeQuery(id+"F15.imprint","IMPRINT",FACE,{"disambiguationData":[TD([[makeQuery(id+"F15.imprint","IMPRINT",EDGE,{"derivedFrom":subQ0}),-1.0]])]});}
            var Q3;
            {var subQ0=sQuery(id+"F15.wireOp",EDGE,"E80");Q3=makeQuery(id+"F15.imprint","IMPRINT",FACE,{"disambiguationData":[TD([[makeQuery(id+"F15.imprint","IMPRINT",EDGE,{"derivedFrom":subQ0}),-1.0]])]});}
            var Q4;
            {var subQ0=sQuery(id+"F15.wireOp",EDGE,"E82");Q4=makeQuery(id+"F15.imprint","IMPRINT",FACE,{"disambiguationData":[TD([[makeQuery(id+"F15.imprint","IMPRINT",EDGE,{"derivedFrom":subQ0}),1.0]])]});}
            var Q5;
            {var subQ0=sQuery(id+"F15.wireOp",EDGE,"E84");Q5=makeQuery(id+"F15.imprint","IMPRINT",FACE,{"disambiguationData":[TD([[makeQuery(id+"F15.imprint","IMPRINT",EDGE,{"derivedFrom":subQ0}),-1.0]])]});}
            var Q6;
            {var subQ3=sQuery(id+"F15.wireOp",EDGE,"E87");Q6=makeQuery(id+"F15.imprint","IMPRINT",FACE,{"disambiguationData":[TD([[makeQuery(id+"F15.imprint","IMPRINT",EDGE,{"derivedFrom":subQ3}),-1.0]])]});}
            var Q7;
            {var subQ0=sQuery(id+"F15.wireOp",EDGE,"E88");Q7=makeQuery(id+"F15.imprint","IMPRINT",FACE,{"disambiguationData":[TD([[makeQuery(id+"F15.imprint","IMPRINT",EDGE,{"derivedFrom":subQ0}),1.0]])]});}
            var Q8;
            {var subQ0=sQuery(id+"F15.wireOp",EDGE,"E90");Q8=makeQuery(id+"F15.imprint","IMPRINT",FACE,{"disambiguationData":[TD([[makeQuery(id+"F15.imprint","IMPRINT",EDGE,{"derivedFrom":subQ0}),1.0]])]});}
            extrude(context, id + "F16", {"entities" : qUnion([Q0, Q1, Q2, Q3, Q4, Q5, Q6, Q7, Q8]), "operationType" : NewBodyOperationType.ADD, "depth" : 12.7 * mm});
        }
        {
            var Q0;
            Q0=makeQuery(id+"F2.opExtrude","CAP_FACE",FACE,{"disambiguationData":[OSD([sQuery(id+"F0.wireOp",EDGE,"E3")])],"isStart":false});
            var sketch = newSketch(context, id + "F17", { "sketchPlane" : qUnion([Q0])});
            skCircle(sketch, "E92", {"center": v(-131.16, -89.38) * mm, "radius": 43.18 * mm});
            skLineSegment(sketch, "E93", {"start": v(-105.97, -54.31) * mm, "end": v(-101.52, -48.12) * mm});
            skLineSegment(sketch, "E94", {"start": v(-93.8, -67.73) * mm, "end": v(-87.21, -63.9) * mm});
            skLineSegment(sketch, "E95", {"start": v(-113.65, -41.7) * mm, "end": v(-116.28, -48.85) * mm});
            skLineSegment(sketch, "E96", {"start": v(-135, -38.73) * mm, "end": v(-134.43, -46.32) * mm});
            skLineSegment(sketch, "E97", {"start": v(-148.43, -41.6) * mm, "end": v(-145.84, -48.77) * mm});
            skLineSegment(sketch, "E98", {"start": v(-166.68, -53.07) * mm, "end": v(-161.36, -58.51) * mm});
            skLineSegment(sketch, "E99", {"start": v(-175.11, -63.9) * mm, "end": v(-168.52, -67.73) * mm});
            skLineSegment(sketch, "E100", {"start": v(-181.72, -84.42) * mm, "end": v(-174.13, -85.17) * mm});
            skLineSegment(sketch, "E101", {"start": v(-173.7, -96.83) * mm, "end": v(-181.2, -98.14) * mm});
            skLineSegment(sketch, "E102", {"start": v(-173.06, -118.1) * mm, "end": v(-166.77, -113.8) * mm});
            skLineSegment(sketch, "E103", {"start": v(-163.84, -128.28) * mm, "end": v(-158.94, -122.44) * mm});
            skLineSegment(sketch, "E104", {"start": v(-142.72, -130.98) * mm, "end": v(-144.76, -138.32) * mm});
            skLineSegment(sketch, "E105", {"start": v(-131.16, -132.56) * mm, "end": v(-131.16, -141.3) * mm});
            skLineSegment(sketch, "E106", {"start": v(-113.25, -128.67) * mm, "end": v(-110.1, -135.6) * mm});
            skLineSegment(sketch, "E107", {"start": v(-103.39, -122.44) * mm, "end": v(-98.48, -128.28) * mm});
            skLineSegment(sketch, "E108", {"start": v(-92.18, -107.95) * mm, "end": v(-85.3, -111.22) * mm});
            skLineSegment(sketch, "E109", {"start": v(-88.63, -96.83) * mm, "end": v(-81.12, -98.14) * mm});
            skLineSegment(sketch, "E110", {"start": v(-89.37, -78.52) * mm, "end": v(-82, -76.6) * mm});
            skSolve(sketch);
        }
        {
            var Q0;
            {var subQ0=sQuery(id+"F17.wireOp",EDGE,"E97");Q0=makeQuery(id+"F17.imprint","IMPRINT",FACE,{"disambiguationData":[TD([[makeQuery(id+"F17.imprint","IMPRINT",EDGE,{"derivedFrom":subQ0}),-1.0]])]});}
            var Q1;
            {var subQ0=sQuery(id+"F17.wireOp",EDGE,"E99");Q1=makeQuery(id+"F17.imprint","IMPRINT",FACE,{"disambiguationData":[TD([[makeQuery(id+"F17.imprint","IMPRINT",EDGE,{"derivedFrom":subQ0}),-1.0]])]});}
            var Q2;
            {var subQ0=sQuery(id+"F17.wireOp",EDGE,"E101");Q2=makeQuery(id+"F17.imprint","IMPRINT",FACE,{"disambiguationData":[TD([[makeQuery(id+"F17.imprint","IMPRINT",EDGE,{"derivedFrom":subQ0}),1.0]])]});}
            var Q3;
            {var subQ0=sQuery(id+"F17.wireOp",EDGE,"E103");Q3=makeQuery(id+"F17.imprint","IMPRINT",FACE,{"disambiguationData":[TD([[makeQuery(id+"F17.imprint","IMPRINT",EDGE,{"derivedFrom":subQ0}),-1.0]])]});}
            var Q4;
            {var subQ3=sQuery(id+"F17.wireOp",EDGE,"E106");Q4=makeQuery(id+"F17.imprint","IMPRINT",FACE,{"disambiguationData":[TD([[makeQuery(id+"F17.imprint","IMPRINT",EDGE,{"derivedFrom":subQ3}),-1.0]])]});}
            var Q5;
            {var subQ0=sQuery(id+"F17.wireOp",EDGE,"E107");Q5=makeQuery(id+"F17.imprint","IMPRINT",FACE,{"disambiguationData":[TD([[makeQuery(id+"F17.imprint","IMPRINT",EDGE,{"derivedFrom":subQ0}),1.0]])]});}
            var Q6;
            {var subQ0=sQuery(id+"F17.wireOp",EDGE,"E109");Q6=makeQuery(id+"F17.imprint","IMPRINT",FACE,{"disambiguationData":[TD([[makeQuery(id+"F17.imprint","IMPRINT",EDGE,{"derivedFrom":subQ0}),1.0]])]});}
            var Q7;
            {var subQ0=sQuery(id+"F17.wireOp",EDGE,"E93");Q7=makeQuery(id+"F17.imprint","IMPRINT",FACE,{"disambiguationData":[TD([[makeQuery(id+"F17.imprint","IMPRINT",EDGE,{"derivedFrom":subQ0}),-1.0]])]});}
            var Q8;
            {var subQ0=sQuery(id+"F17.wireOp",EDGE,"E95");Q8=makeQuery(id+"F17.imprint","IMPRINT",FACE,{"disambiguationData":[TD([[makeQuery(id+"F17.imprint","IMPRINT",EDGE,{"derivedFrom":subQ0}),-1.0]])]});}
            extrude(context, id + "F18", {"entities" : qUnion([Q0, Q1, Q2, Q3, Q4, Q5, Q6, Q7, Q8]), "operationType" : NewBodyOperationType.ADD, "depth" : 12.7 * mm});
        }
        {
            var Q0;
            Q0=makeQuery(id+"F2.opExtrude","CAP_FACE",FACE,{"disambiguationData":[OSD([sQuery(id+"F0.wireOp",EDGE,"E4")])],"isStart":false});
            var sketch = newSketch(context, id + "F19", { "sketchPlane" : qUnion([Q0])});
            skCircle(sketch, "E111", {"center": v(376.84, -89.38) * mm, "radius": 43.18 * mm});
            skLineSegment(sketch, "E112", {"start": v(402.03, -54.31) * mm, "end": v(406.48, -48.12) * mm});
            skLineSegment(sketch, "E113", {"start": v(414.2, -67.73) * mm, "end": v(420.79, -63.9) * mm});
            skLineSegment(sketch, "E114", {"start": v(394.35, -41.7) * mm, "end": v(391.72, -48.85) * mm});
            skLineSegment(sketch, "E115", {"start": v(373, -38.73) * mm, "end": v(373.57, -46.32) * mm});
            skLineSegment(sketch, "E116", {"start": v(359.57, -41.6) * mm, "end": v(362.16, -48.77) * mm});
            skLineSegment(sketch, "E117", {"start": v(341.32, -53.07) * mm, "end": v(346.64, -58.51) * mm});
            skLineSegment(sketch, "E118", {"start": v(332.89, -63.9) * mm, "end": v(339.48, -67.73) * mm});
            skLineSegment(sketch, "E119", {"start": v(326.28, -84.42) * mm, "end": v(333.87, -85.17) * mm});
            skLineSegment(sketch, "E120", {"start": v(334.3, -96.83) * mm, "end": v(326.8, -98.14) * mm});
            skLineSegment(sketch, "E121", {"start": v(334.94, -118.1) * mm, "end": v(341.23, -113.8) * mm});
            skLineSegment(sketch, "E122", {"start": v(344.16, -128.28) * mm, "end": v(349.06, -122.44) * mm});
            skLineSegment(sketch, "E123", {"start": v(365.28, -130.98) * mm, "end": v(363.24, -138.32) * mm});
            skLineSegment(sketch, "E124", {"start": v(376.84, -132.56) * mm, "end": v(376.84, -142.71) * mm});
            skLineSegment(sketch, "E125", {"start": v(394.75, -128.67) * mm, "end": v(397.9, -135.6) * mm});
            skLineSegment(sketch, "E126", {"start": v(404.61, -122.44) * mm, "end": v(409.52, -128.28) * mm});
            skLineSegment(sketch, "E127", {"start": v(415.82, -107.95) * mm, "end": v(422.7, -111.22) * mm});
            skLineSegment(sketch, "E128", {"start": v(419.37, -96.83) * mm, "end": v(426.88, -98.14) * mm});
            skLineSegment(sketch, "E129", {"start": v(418.63, -78.52) * mm, "end": v(426, -76.6) * mm});
            skSolve(sketch);
        }
        {
            var Q0;
            {var subQ0=sQuery(id+"F19.wireOp",EDGE,"E116");Q0=makeQuery(id+"F19.imprint","IMPRINT",FACE,{"disambiguationData":[TD([[makeQuery(id+"F19.imprint","IMPRINT",EDGE,{"derivedFrom":subQ0}),-1.0]])]});}
            var Q1;
            {var subQ0=sQuery(id+"F19.wireOp",EDGE,"E118");Q1=makeQuery(id+"F19.imprint","IMPRINT",FACE,{"disambiguationData":[TD([[makeQuery(id+"F19.imprint","IMPRINT",EDGE,{"derivedFrom":subQ0}),-1.0]])]});}
            var Q2;
            {var subQ0=sQuery(id+"F19.wireOp",EDGE,"E120");Q2=makeQuery(id+"F19.imprint","IMPRINT",FACE,{"disambiguationData":[TD([[makeQuery(id+"F19.imprint","IMPRINT",EDGE,{"derivedFrom":subQ0}),1.0]])]});}
            var Q3;
            {var subQ0=sQuery(id+"F19.wireOp",EDGE,"E122");Q3=makeQuery(id+"F19.imprint","IMPRINT",FACE,{"disambiguationData":[TD([[makeQuery(id+"F19.imprint","IMPRINT",EDGE,{"derivedFrom":subQ0}),-1.0]])]});}
            var Q4;
            {var subQ3=sQuery(id+"F19.wireOp",EDGE,"E125");Q4=makeQuery(id+"F19.imprint","IMPRINT",FACE,{"disambiguationData":[TD([[makeQuery(id+"F19.imprint","IMPRINT",EDGE,{"derivedFrom":subQ3}),-1.0]])]});}
            var Q5;
            {var subQ0=sQuery(id+"F19.wireOp",EDGE,"E126");Q5=makeQuery(id+"F19.imprint","IMPRINT",FACE,{"disambiguationData":[TD([[makeQuery(id+"F19.imprint","IMPRINT",EDGE,{"derivedFrom":subQ0}),1.0]])]});}
            var Q6;
            {var subQ0=sQuery(id+"F19.wireOp",EDGE,"E128");Q6=makeQuery(id+"F19.imprint","IMPRINT",FACE,{"disambiguationData":[TD([[makeQuery(id+"F19.imprint","IMPRINT",EDGE,{"derivedFrom":subQ0}),1.0]])]});}
            var Q7;
            {var subQ0=sQuery(id+"F19.wireOp",EDGE,"E112");Q7=makeQuery(id+"F19.imprint","IMPRINT",FACE,{"disambiguationData":[TD([[makeQuery(id+"F19.imprint","IMPRINT",EDGE,{"derivedFrom":subQ0}),-1.0]])]});}
            var Q8;
            {var subQ0=sQuery(id+"F19.wireOp",EDGE,"E114");Q8=makeQuery(id+"F19.imprint","IMPRINT",FACE,{"disambiguationData":[TD([[makeQuery(id+"F19.imprint","IMPRINT",EDGE,{"derivedFrom":subQ0}),-1.0]])]});}
            extrude(context, id + "F20", {"entities" : qUnion([Q0, Q1, Q2, Q3, Q4, Q5, Q6, Q7, Q8]), "operationType" : NewBodyOperationType.ADD, "depth" : 12.7 * mm});
        }
        {
            var Q0;
            {var subQ0=sQuery(id+"F0.wireOp",EDGE,"E5.left");var subQ5=sQuery(id+"F0.wireOp",EDGE,"E6");var subQ6=makeQuery(id+"F0.imprint","INTERSECT",VERTEX,{"derivedFrom":[subQ0,subQ5]});Q0=makeQuery(id+"F0.imprint","IMPRINT",FACE,{"disambiguationData":[TD([[makeQuery(id+"F0.imprint","IMPRINT",EDGE,{"disambiguationData":[TD([[subQ6,1.0]])],"derivedFrom":subQ5}),-1.0]])]});}
            var Q1;
            {var subQ0=sQuery(id+"F0.wireOp",EDGE,"E6");var subQ1=sQuery(id+"F0.wireOp",EDGE,"E5.top");var subQ2=makeQuery(id+"F0.imprint","INTERSECT",VERTEX,{"derivedFrom":[subQ1,subQ0]});Q1=makeQuery(id+"F0.imprint","IMPRINT",FACE,{"disambiguationData":[TD([[makeQuery(id+"F0.imprint","IMPRINT",EDGE,{"disambiguationData":[TD([[subQ2,-1.0]])],"derivedFrom":subQ1}),1.0]])]});}
            var Q2;
            {var subQ0=sQuery(id+"F0.wireOp",EDGE,"E5.right");var subQ5=sQuery(id+"F0.wireOp",EDGE,"E7");var subQ6=makeQuery(id+"F0.imprint","INTERSECT",VERTEX,{"derivedFrom":[subQ0,subQ5]});Q2=makeQuery(id+"F0.imprint","IMPRINT",FACE,{"disambiguationData":[TD([[makeQuery(id+"F0.imprint","IMPRINT",EDGE,{"disambiguationData":[TD([[subQ6,-1.0]])],"derivedFrom":subQ5}),-1.0]])]});}
            extrude(context, id + "F21", {"entities" : qUnion([Q0, Q1, Q2]), "operationType" : NewBodyOperationType.ADD, "depth" : 114.3 * mm});
        }
        {
            var Q0;
            {var subQ0=sQuery(id+"F0.wireOp",EDGE,"E5.left");var subQ1=sQuery(id+"F0.wireOp",EDGE,"E5.top");var subQ2=makeQuery(id+"F0.imprint","INTERSECT",VERTEX,{"derivedFrom":[subQ1,subQ0]});Q0=makeQuery(id+"F0.imprint","IMPRINT",FACE,{"disambiguationData":[TD([[makeQuery(id+"F0.imprint","IMPRINT",EDGE,{"disambiguationData":[TD([[subQ2,-1.0]])],"derivedFrom":subQ1}),-1.0]])]});}
            var Q1;
            {var subQ0=sQuery(id+"F0.wireOp",EDGE,"E8.top");var subQ1=sQuery(id+"F0.wireOp",EDGE,"E6");var subQ2=makeQuery(id+"F0.imprint","INTERSECT",VERTEX,{"derivedFrom":[subQ1,subQ0]});Q1=makeQuery(id+"F0.imprint","IMPRINT",FACE,{"disambiguationData":[TD([[makeQuery(id+"F0.imprint","IMPRINT",EDGE,{"disambiguationData":[TD([[subQ2,-1.0]])],"derivedFrom":subQ1}),1.0]])]});}
            var Q2;
            {var subQ1=sQuery(id+"F0.wireOp",EDGE,"E5.top");var subQ5=sQuery(id+"F0.wireOp",EDGE,"E5.left");var subQ6=makeQuery(id+"F0.imprint","INTERSECT",VERTEX,{"derivedFrom":[subQ1,subQ5]});Q2=makeQuery(id+"F0.imprint","IMPRINT",FACE,{"disambiguationData":[TD([[makeQuery(id+"F0.imprint","IMPRINT",EDGE,{"disambiguationData":[TD([[subQ6,-1.0]])],"derivedFrom":subQ1}),1.0]])]});}
            var Q3;
            {var subQ0=sQuery(id+"F0.wireOp",EDGE,"E5.right");var subQ1=sQuery(id+"F0.wireOp",EDGE,"E5.top");var subQ2=makeQuery(id+"F0.imprint","INTERSECT",VERTEX,{"derivedFrom":[subQ1,subQ0]});Q3=makeQuery(id+"F0.imprint","IMPRINT",FACE,{"disambiguationData":[TD([[makeQuery(id+"F0.imprint","IMPRINT",EDGE,{"disambiguationData":[TD([[subQ2,1.0]])],"derivedFrom":subQ1}),-1.0]])]});}
            var Q4;
            {var subQ1=sQuery(id+"F0.wireOp",EDGE,"E5.top");var subQ5=sQuery(id+"F0.wireOp",EDGE,"E5.right");var subQ9=makeQuery(id+"F0.imprint","INTERSECT",VERTEX,{"derivedFrom":[subQ1,subQ5]});Q4=makeQuery(id+"F0.imprint","IMPRINT",FACE,{"disambiguationData":[TD([[makeQuery(id+"F0.imprint","IMPRINT",EDGE,{"disambiguationData":[TD([[subQ9,1.0]])],"derivedFrom":subQ1}),1.0]])]});}
            var Q5;
            {var subQ0=sQuery(id+"F0.wireOp",EDGE,"E8.right");var subQ1=sQuery(id+"F0.wireOp",EDGE,"E7");var subQ2=makeQuery(id+"F0.imprint","INTERSECT",VERTEX,{"derivedFrom":[subQ1,subQ0]});Q5=makeQuery(id+"F0.imprint","IMPRINT",FACE,{"disambiguationData":[TD([[makeQuery(id+"F0.imprint","IMPRINT",EDGE,{"disambiguationData":[TD([[subQ2,-1.0]])],"derivedFrom":subQ1}),1.0]])]});}
            extrude(context, id + "F22", {"entities" : qUnion([Q0, Q1, Q2, Q3, Q4, Q5]), "depth" : 133.35 * mm});
        }
        {
            var Q0;
            Q0=makeQuery(id+"F21.opExtrude","SWEPT_FACE",FACE,{"disambiguationData":[OSD([sQuery(id+"F0.wireOp",EDGE,"E5.top")])]});
            var sketch = newSketch(context, id + "F23", { "sketchPlane" : qUnion([Q0])});
            skLineSegment(sketch, "E130", {"start": v(84.74, 57.15) * mm, "end": v(84.74, 0) * mm});
            skLineSegment(sketch, "E131", {"start": v(160.94, 57.15) * mm, "end": v(160.94, 0) * mm});
            skArc(sketch, "E132", {"start": v(160.94, 57.15) * mm, "mid": v(122.84, 95.25) * mm, "end": v(84.74, 57.15) * mm});
            skLineSegment(sketch, "E133", {"start": v(84.74, 6.35) * mm, "end": v(160.94, 6.35) * mm});
            skSolve(sketch);
        }
        {
            var Q0;
            {var subQ0=sQuery(id+"F23.wireOp",EDGE,"E132");Q0=makeQuery(id+"F23.imprint","IMPRINT",FACE,{"disambiguationData":[TD([[makeQuery(id+"F23.imprint","IMPRINT",EDGE,{"derivedFrom":subQ0}),1.0]])]});}
            extrude(context, id + "F24", {"entities" : qUnion([Q0]), "operationType" : NewBodyOperationType.REMOVE, "oppositeDirection" : true, "depth" : 12.7 * mm});
        }
        {
            var Q0;
            {var subQ0=sQuery(id+"F0.wireOp",EDGE,"E8.left");var subQ1=sQuery(id+"F0.wireOp",EDGE,"E5.left");var subQ2=sQuery(id+"F0.wireOp",EDGE,"E5.bottom");var subQ5=sQuery(id+"F0.wireOp",EDGE,"E3");var subQ6=sQuery(id+"F3.wireOp",EDGE,"E17");var subQ7=sQuery(id+"F3.wireOp",EDGE,"E9");var subQ8=sQuery(id+"F3.wireOp",EDGE,"E16");Q0=makeQuery(id+"F21.boolean.opBoolean","MERGE",FACE,{"derivedFrom":[makeQuery(id+"F6.boolean.opBoolean","SPLIT",FACE,{"disambiguationData":[TD([makeQuery(id+"F4.opExtrude","SWEPT_FACE",FACE,{"disambiguationData":[OSD([subQ6])]})])],"derivedFrom":makeQuery(id+"F4.opExtrude","CAP_FACE",FACE,{"disambiguationData":[OSD([subQ5,subQ7,subQ8,subQ6])],"isStart":false})}),makeQuery(id+"F21.opExtrude","CAP_FACE",FACE,{"disambiguationData":[OSD([subQ2,subQ1,sQuery(id+"F0.wireOp",EDGE,"E6"),subQ0])],"isStart":false})]});}
            var sketch = newSketch(context, id + "F25", { "sketchPlane" : qUnion([Q0])});
            skLineSegment(sketch, "E134.bottom", {"start": v(33.94, -89.38) * mm, "end": v(21.24, -89.38) * mm});
            skLineSegment(sketch, "E134.top", {"start": v(33.94, -108.43) * mm, "end": v(21.24, -108.43) * mm});
            skLineSegment(sketch, "E134.left", {"start": v(33.94, -89.38) * mm, "end": v(33.94, -108.43) * mm});
            skLineSegment(sketch, "E134.right", {"start": v(21.24, -89.38) * mm, "end": v(21.24, -108.43) * mm});
            skLineSegment(sketch, "E135.bottom", {"start": v(33.94, -114.78) * mm, "end": v(21.24, -114.78) * mm});
            skLineSegment(sketch, "E135.top", {"start": v(33.94, -133.83) * mm, "end": v(21.24, -133.83) * mm});
            skLineSegment(sketch, "E135.left", {"start": v(33.94, -114.78) * mm, "end": v(33.94, -133.83) * mm});
            skLineSegment(sketch, "E135.right", {"start": v(21.24, -114.78) * mm, "end": v(21.24, -133.83) * mm});
            skLineSegment(sketch, "E136.bottom", {"start": v(33.94, -140.18) * mm, "end": v(21.24, -140.18) * mm});
            skLineSegment(sketch, "E136.top", {"start": v(33.94, -159.23) * mm, "end": v(21.24, -159.23) * mm});
            skLineSegment(sketch, "E136.left", {"start": v(33.94, -140.18) * mm, "end": v(33.94, -159.23) * mm});
            skLineSegment(sketch, "E136.right", {"start": v(21.24, -140.18) * mm, "end": v(21.24, -159.23) * mm});
            skSolve(sketch);
        }
        {
            var Q0;
            Q0=makeQuery(id+"F21.opExtrude","CAP_FACE",FACE,{"disambiguationData":[OSD([sQuery(id+"F0.wireOp",EDGE,"E5.top"),sQuery(id+"F0.wireOp",EDGE,"E6"),sQuery(id+"F0.wireOp",EDGE,"E7"),sQuery(id+"F0.wireOp",EDGE,"E8.top")])],"isStart":false});
            var sketch = newSketch(context, id + "F26", { "sketchPlane" : qUnion([Q0])});
            skLineSegment(sketch, "E137.bottom", {"start": v(65.69, -190.98) * mm, "end": v(84.74, -190.98) * mm});
            skLineSegment(sketch, "E137.top", {"start": v(65.69, -203.68) * mm, "end": v(84.74, -203.68) * mm});
            skLineSegment(sketch, "E137.left", {"start": v(65.69, -190.98) * mm, "end": v(65.69, -203.68) * mm});
            skLineSegment(sketch, "E137.right", {"start": v(84.74, -190.98) * mm, "end": v(84.74, -203.68) * mm});
            skLineSegment(sketch, "E138.bottom", {"start": v(97.44, -190.98) * mm, "end": v(116.49, -190.98) * mm});
            skLineSegment(sketch, "E138.top", {"start": v(97.44, -203.68) * mm, "end": v(116.49, -203.68) * mm});
            skLineSegment(sketch, "E138.left", {"start": v(97.44, -190.98) * mm, "end": v(97.44, -203.68) * mm});
            skLineSegment(sketch, "E138.right", {"start": v(116.49, -190.98) * mm, "end": v(116.49, -203.68) * mm});
            skLineSegment(sketch, "E139.bottom", {"start": v(129.19, -190.98) * mm, "end": v(148.24, -190.98) * mm});
            skLineSegment(sketch, "E139.top", {"start": v(129.19, -203.68) * mm, "end": v(148.24, -203.68) * mm});
            skLineSegment(sketch, "E139.left", {"start": v(129.19, -190.98) * mm, "end": v(129.19, -203.68) * mm});
            skLineSegment(sketch, "E139.right", {"start": v(148.24, -190.98) * mm, "end": v(148.24, -203.68) * mm});
            skLineSegment(sketch, "E140.bottom", {"start": v(160.94, -190.98) * mm, "end": v(179.99, -190.98) * mm});
            skLineSegment(sketch, "E140.top", {"start": v(160.94, -203.68) * mm, "end": v(179.99, -203.68) * mm});
            skLineSegment(sketch, "E140.left", {"start": v(160.94, -190.98) * mm, "end": v(160.94, -203.68) * mm});
            skLineSegment(sketch, "E140.right", {"start": v(179.99, -190.98) * mm, "end": v(179.99, -203.68) * mm});
            skSolve(sketch);
        }
        {
            var Q0;
            {var subQ0=sQuery(id+"F0.wireOp",EDGE,"E8.right");var subQ1=sQuery(id+"F0.wireOp",EDGE,"E5.right");var subQ2=sQuery(id+"F0.wireOp",EDGE,"E5.bottom");var subQ3=sQuery(id+"F3.wireOp",EDGE,"E18");var subQ4=sQuery(id+"F3.wireOp",EDGE,"E9");var subQ5=sQuery(id+"F0.wireOp",EDGE,"E4");var subQ8=sQuery(id+"F3.wireOp",EDGE,"E19");Q0=makeQuery(id+"F21.boolean.opBoolean","MERGE",FACE,{"derivedFrom":[makeQuery(id+"F6.boolean.opBoolean","SPLIT",FACE,{"disambiguationData":[TD([makeQuery(id+"F4.opExtrude","SWEPT_FACE",FACE,{"disambiguationData":[OSD([subQ3])]})])],"derivedFrom":makeQuery(id+"F4.opExtrude","CAP_FACE",FACE,{"disambiguationData":[OSD([subQ5,subQ4,subQ3,subQ8])],"isStart":false})}),makeQuery(id+"F21.opExtrude","CAP_FACE",FACE,{"disambiguationData":[OSD([subQ2,subQ1,sQuery(id+"F0.wireOp",EDGE,"E7"),subQ0])],"isStart":false})]});}
            var sketch = newSketch(context, id + "F27", { "sketchPlane" : qUnion([Q0])});
            skLineSegment(sketch, "E141.bottom", {"start": v(211.74, -159.23) * mm, "end": v(224.44, -159.23) * mm});
            skLineSegment(sketch, "E141.top", {"start": v(211.74, -140.18) * mm, "end": v(224.44, -140.18) * mm});
            skLineSegment(sketch, "E141.left", {"start": v(211.74, -159.23) * mm, "end": v(211.74, -140.18) * mm});
            skLineSegment(sketch, "E141.right", {"start": v(224.44, -159.23) * mm, "end": v(224.44, -140.18) * mm});
            skLineSegment(sketch, "E142.bottom", {"start": v(211.74, -133.83) * mm, "end": v(224.44, -133.83) * mm});
            skLineSegment(sketch, "E142.top", {"start": v(211.74, -114.78) * mm, "end": v(224.44, -114.78) * mm});
            skLineSegment(sketch, "E142.left", {"start": v(211.74, -133.83) * mm, "end": v(211.74, -114.78) * mm});
            skLineSegment(sketch, "E142.right", {"start": v(224.44, -133.83) * mm, "end": v(224.44, -114.78) * mm});
            skLineSegment(sketch, "E143.bottom", {"start": v(211.74, -108.43) * mm, "end": v(224.44, -108.43) * mm});
            skLineSegment(sketch, "E143.top", {"start": v(211.74, -89.38) * mm, "end": v(224.44, -89.38) * mm});
            skLineSegment(sketch, "E143.left", {"start": v(211.74, -108.43) * mm, "end": v(211.74, -89.38) * mm});
            skLineSegment(sketch, "E143.right", {"start": v(224.44, -108.43) * mm, "end": v(224.44, -89.38) * mm});
            skSolve(sketch);
        }
        {
            var Q0;
            Q0=makeQuery(id+"F25.imprint","IMPRINT",FACE,{"disambiguationData":[TD([[makeQuery(id+"F25.imprint","IMPRINT",EDGE,{"derivedFrom":sQuery(id+"F25.wireOp",EDGE,"E134.bottom")}),1.0]])]});
            var Q1;
            Q1=makeQuery(id+"F25.imprint","IMPRINT",FACE,{"disambiguationData":[TD([[makeQuery(id+"F25.imprint","IMPRINT",EDGE,{"derivedFrom":sQuery(id+"F25.wireOp",EDGE,"E135.bottom")}),1.0]])]});
            var Q2;
            Q2=makeQuery(id+"F25.imprint","IMPRINT",FACE,{"disambiguationData":[TD([[makeQuery(id+"F25.imprint","IMPRINT",EDGE,{"derivedFrom":sQuery(id+"F25.wireOp",EDGE,"E136.bottom")}),1.0]])]});
            var Q3;
            Q3=makeQuery(id+"F26.imprint","IMPRINT",FACE,{"disambiguationData":[TD([[makeQuery(id+"F26.imprint","IMPRINT",EDGE,{"derivedFrom":sQuery(id+"F26.wireOp",EDGE,"E137.bottom")}),-1.0]])]});
            var Q4;
            Q4=makeQuery(id+"F26.imprint","IMPRINT",FACE,{"disambiguationData":[TD([[makeQuery(id+"F26.imprint","IMPRINT",EDGE,{"derivedFrom":sQuery(id+"F26.wireOp",EDGE,"E138.bottom")}),-1.0]])]});
            var Q5;
            Q5=makeQuery(id+"F26.imprint","IMPRINT",FACE,{"disambiguationData":[TD([[makeQuery(id+"F26.imprint","IMPRINT",EDGE,{"derivedFrom":sQuery(id+"F26.wireOp",EDGE,"E139.bottom")}),-1.0]])]});
            var Q6;
            Q6=makeQuery(id+"F26.imprint","IMPRINT",FACE,{"disambiguationData":[TD([[makeQuery(id+"F26.imprint","IMPRINT",EDGE,{"derivedFrom":sQuery(id+"F26.wireOp",EDGE,"E140.bottom")}),-1.0]])]});
            var Q7;
            Q7=makeQuery(id+"F27.imprint","IMPRINT",FACE,{"disambiguationData":[TD([[makeQuery(id+"F27.imprint","IMPRINT",EDGE,{"derivedFrom":sQuery(id+"F27.wireOp",EDGE,"E141.bottom")}),1.0]])]});
            var Q8;
            Q8=makeQuery(id+"F27.imprint","IMPRINT",FACE,{"disambiguationData":[TD([[makeQuery(id+"F27.imprint","IMPRINT",EDGE,{"derivedFrom":sQuery(id+"F27.wireOp",EDGE,"E142.bottom")}),1.0]])]});
            var Q9;
            Q9=makeQuery(id+"F27.imprint","IMPRINT",FACE,{"disambiguationData":[TD([[makeQuery(id+"F27.imprint","IMPRINT",EDGE,{"derivedFrom":sQuery(id+"F27.wireOp",EDGE,"E143.bottom")}),1.0]])]});
            extrude(context, id + "F28", {"entities" : qUnion([Q0, Q1, Q2, Q3, Q4, Q5, Q6, Q7, Q8, Q9]), "depth" : 7.62 * mm});
        }
        {
            var Q0;
            Q0=makeQuery(id+"F4.opExtrude","SWEPT_EDGE",EDGE,{"disambiguationData":[OSD([sQuery(id+"F3.wireOp",EDGE,"E18"),sQuery(id+"F3.wireOp",EDGE,"E19")])]});
            var Q1;
            Q1=makeQuery(id+"F4.opExtrude","SWEPT_EDGE",EDGE,{"disambiguationData":[OSD([sQuery(id+"F3.wireOp",EDGE,"E16"),sQuery(id+"F3.wireOp",EDGE,"E17")])]});
            fillet(context, id + "F29", {"entities" : qUnion([Q0, Q1]), "radius" : 7.62 * mm, "tangentPropagation" : true, "allowEdgeOverflow" : false});
        }
    });
